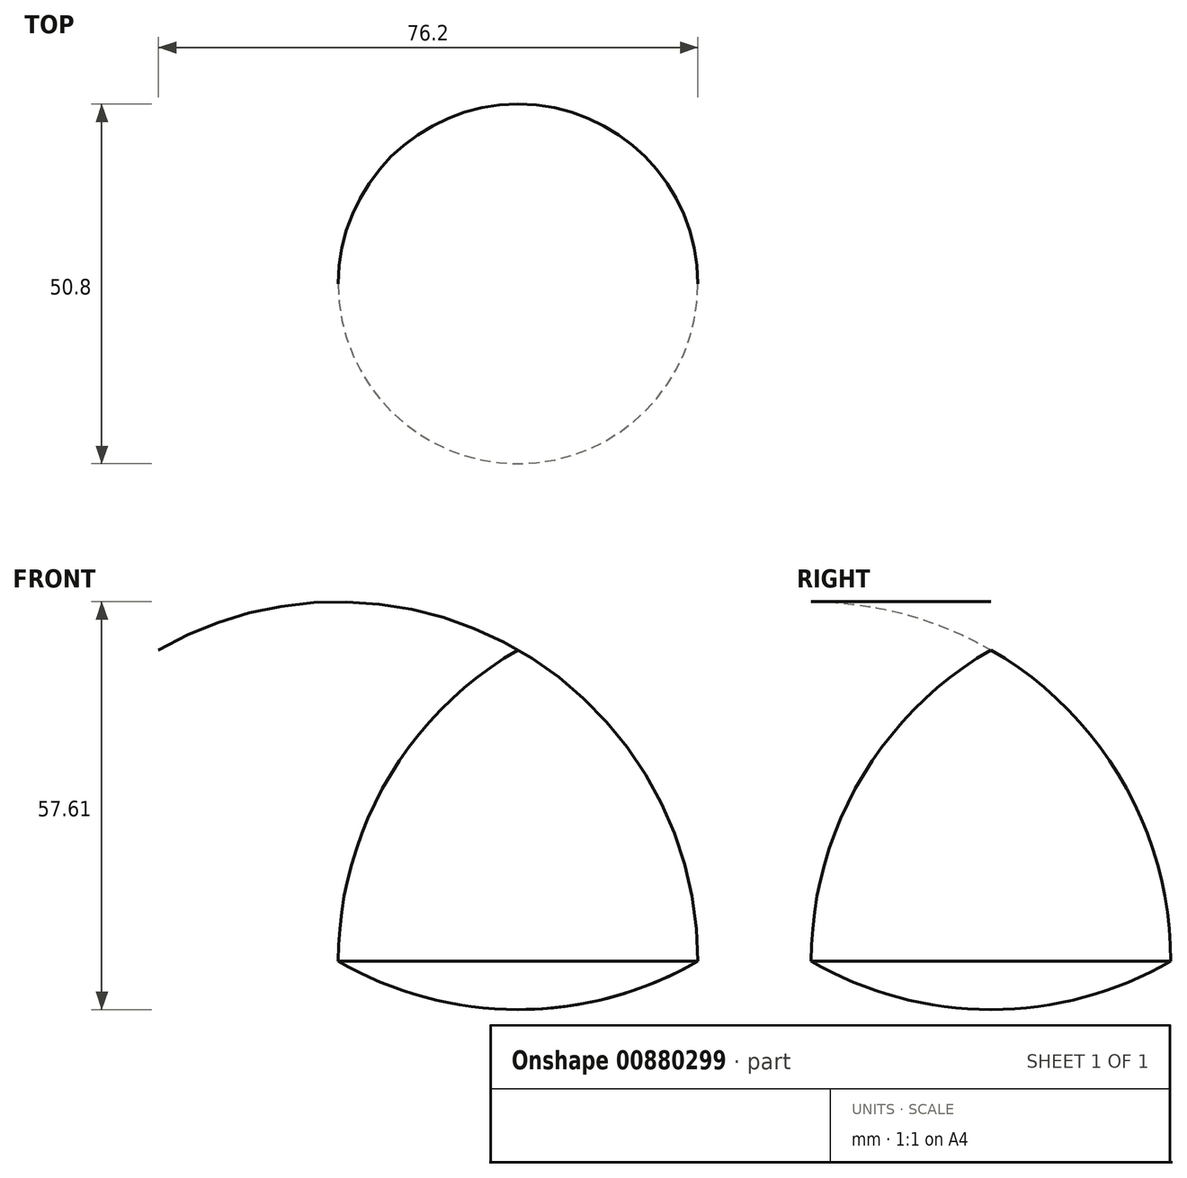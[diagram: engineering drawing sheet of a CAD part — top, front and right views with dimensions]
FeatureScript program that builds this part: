
annotation { "Feature Type Name" : "Feature", "Feature Type Description" : "" }
export const myFeature = defineFeature(function(context is Context, id is Id, definition is map)
    precondition{}
    {
        {
            var Q0;
            Q0=qCreatedBy(makeId("Front.planeOp"),FACE);
            var sketch = newSketch(context, id + "F0", { "sketchPlane" : qUnion([Q0])});
            skArc(sketch, "E0", {"start": v(0, -6.8) * mm, "mid": v(13.15, -5.07) * mm, "end": v(25.4, 0) * mm});
            skArc(sketch, "E1.trimOffspring", {"start": v(25.4, 0) * mm, "mid": v(18.6, 25.4) * mm, "end": v(0, 44) * mm});
            skLineSegment(sketch, "E2", {"start": v(0, 44) * mm, "end": v(0, -6.8) * mm});
            skSolve(sketch);
        }
        {
            var Q0;
            Q0=qCreatedBy(makeId("Front.planeOp"),FACE);
            var sketch = newSketch(context, id + "F1", { "sketchPlane" : qUnion([Q0])});
            skLineSegment(sketch, "E3", {"start": v(0, -13.04) * mm, "end": v(0, 53.76) * mm, "construction": true});
            skSolve(sketch);
        }
        {
            var Q0;
            Q0 = qSketchRegion(id + "F0", true);
            var Q1;
            Q1=sQuery(id+"F1.wireOp",EDGE,"E3");
            revolve(context, id + "F2", {"surfaceOperationType" : NewSurfaceOperationType.NEW, "entities" : qUnion([Q0]), "axis" : qUnion([Q1]), "revolveType" : RevolveType.FULL});
        }
    });
